# Revit family: Indoor 140 types Avec hôte
name_source: partatom
category: Dispositifs d'éclairage
units: mm (PartAtom-declared; Revit-internal decimal feet)

## family parameters
Conserver l'orientation des annotations = Oui
Cote de connecteur circulaire = Utiliser le diamètre
Couper avec des vides une fois chargée = Non
Hôte = Face
Partagée = Non
Point de calcul de pièce = Non
Type d'élément = Normal

## types (4) — shared parameters
Classe = II
Code d'assemblage = D5010200
Elévation par défaut = 110 cm
Fabricant = B.E.G.
Hauteur de montage max = 220 cm
IP = 20
Image du type = MURAL.jpg
Marque = LUXOMAT
Mode de pose = Encastré mural
Position en hauteur = 110 cm
URL = http://www.luxomat.com

## per-type parameters (varying)
| type | Alimentation | Charge Cos ɸ =0.5 | Charge Cos ɸ =1 | Charge LED | Commentaires du type | Consommation | Modèle | Relais | Référence | Température ambiante | Type de Sortie |
| 01- INDOOR 140-EN Générique | 110-240 V AC |  |  |  | INTER.AUTO.BALISAGE LED INTEGRE.120°/8M ENCASTRE MURAL |  | INDOOR 140-EN |  |  | -25°C à +50°C |  |
| 02- INDOOR 140-L-EN réf 94328 | 110-240 V AC | 1000 VA | 2000 W | 250 W | INTER.AUTO.3 FILS.1 CONTACT.BALISAGE LED INTEGRE.120°/8M ENCASTRE MURAL | 0,4 à 0,8 W | INDOOR 140-EN | 10 A | 94328 | -25°C à +50°C | TOR + balisage LED intégré |
| 03- INDOOR 140-L-KNX-DX-EN réf 93393 | 24 V DC par bus KNX | 0 | 0 | 0 | INTER.AUTO.KNX.VERSION DELUXE.BALISAGE LED INTEGRE.120°/8M ENCASTRE MURAL | 12 mA | INDOOR 140-KNX-DX-EN | 0 | 93393 | -5°C à +45°C | KNX - 1 sortie Eclairage TOR ou GRADATION / 3 sorties Présence / Capteur de température |
| 04- INDOOR 140-L-KNXs-DX-EN réf 93526 | 24 V DC par bus KNX | 0 | 0 | 0 | INTER.AUTO.KNX SECURE.VERSION DELUXE.BALISAGE LED INTEGRE.120°/8M ENCASTRE MURAL | 12 mA | INDOOR 140-KNXs-DX-EN | 0 | 93526 | -5°C à +45°C | KNX Sécure - 1 sortie Eclairage TOR ou GRADATION / 3 sorties Présence / Capteur de température / HCL |

## geometry (parser evidence)
native form markers: Blend x10
no freeform markers — native parametric forms only
